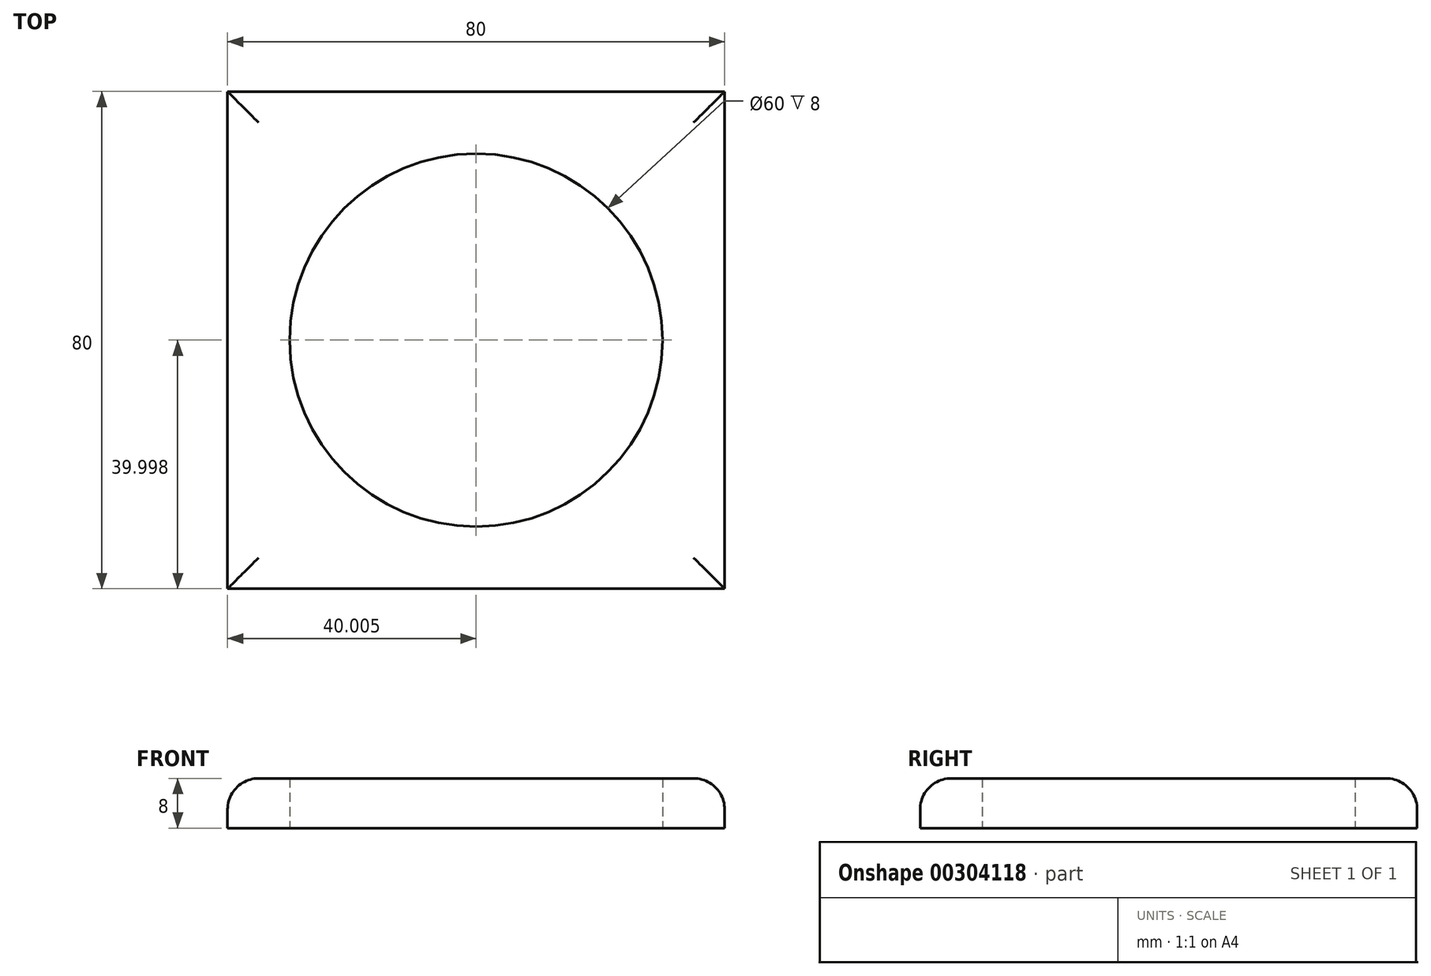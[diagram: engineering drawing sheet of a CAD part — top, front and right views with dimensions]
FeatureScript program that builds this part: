
annotation { "Feature Type Name" : "Feature", "Feature Type Description" : "" }
export const myFeature = defineFeature(function(context is Context, id is Id, definition is map)
    precondition{}
    {
        {
            var Q0;
            Q0=qCreatedBy(makeId("Top.planeOp"),FACE);
            var sketch = newSketch(context, id + "F0", { "sketchPlane" : qUnion([Q0])});
            skLineSegment(sketch, "E0.bottom", {"start": v(-66.84, 48.36) * mm, "end": v(13.16, 48.36) * mm});
            skLineSegment(sketch, "E0.top", {"start": v(-66.84, -31.64) * mm, "end": v(13.16, -31.64) * mm});
            skLineSegment(sketch, "E0.left", {"start": v(-66.84, 48.36) * mm, "end": v(-66.84, -31.64) * mm});
            skLineSegment(sketch, "E0.right", {"start": v(13.16, 48.36) * mm, "end": v(13.16, -31.64) * mm});
            skCircle(sketch, "E1", {"center": v(-26.84, 8.36) * mm, "radius": 30 * mm});
            skSolve(sketch);
        }
        {
            var Q0;
            Q0=makeQuery(id+"F0.imprint","IMPRINT",FACE,{"disambiguationData":[TD([[makeQuery(id+"F0.imprint","IMPRINT",EDGE,{"derivedFrom":sQuery(id+"F0.wireOp",EDGE,"E0.bottom")}),-1.0]])]});
            extrude(context, id + "F1", {"entities" : qUnion([Q0]), "depth" : 8 * mm, "offsetDistance" : 25 * mm});
        }
        {
            var Q0;
            Q0=makeQuery(id+"F1.opExtrude","CAP_EDGE",EDGE,{"disambiguationData":[OSD([sQuery(id+"F0.wireOp",EDGE,"E0.bottom")])],"isStart":false});
            var Q1;
            Q1=makeQuery(id+"F1.opExtrude","CAP_EDGE",EDGE,{"disambiguationData":[OSD([sQuery(id+"F0.wireOp",EDGE,"E0.left")])],"isStart":false});
            var Q2;
            Q2=makeQuery(id+"F1.opExtrude","CAP_EDGE",EDGE,{"disambiguationData":[OSD([sQuery(id+"F0.wireOp",EDGE,"E0.top")])],"isStart":false});
            var Q3;
            Q3=makeQuery(id+"F1.opExtrude","CAP_EDGE",EDGE,{"disambiguationData":[OSD([sQuery(id+"F0.wireOp",EDGE,"E0.right")])],"isStart":false});
            fillet(context, id + "F2", {"entities" : qUnion([Q0, Q1, Q2, Q3]), "radius" : 5 * mm, "tangentPropagation" : true, "allowEdgeOverflow" : false});
        }
    });
